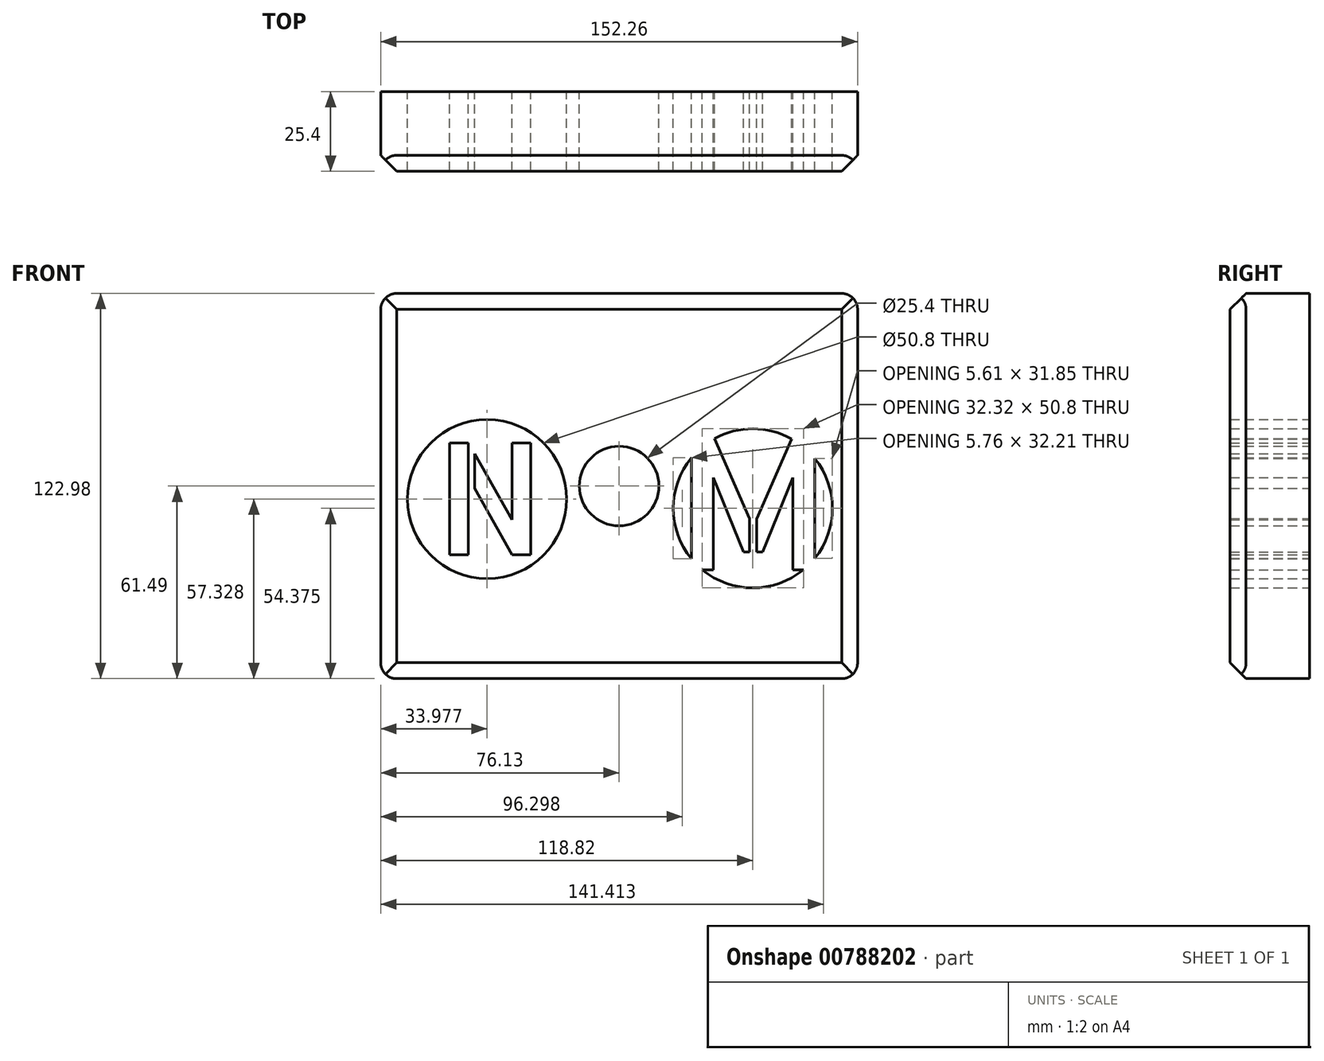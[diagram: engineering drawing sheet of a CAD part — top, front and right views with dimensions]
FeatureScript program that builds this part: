
annotation { "Feature Type Name" : "Feature", "Feature Type Description" : "" }
export const myFeature = defineFeature(function(context is Context, id is Id, definition is map)
    precondition{}
    {
        {
            var Q0;
            Q0=qCreatedBy(makeId("Front.planeOp"),FACE);
            var sketch = newSketch(context, id + "F0", { "sketchPlane" : qUnion([Q0])});
            skLineSegment(sketch, "E0.bottom", {"start": v(-76.13, -61.49) * mm, "end": v(76.13, -61.49) * mm});
            skLineSegment(sketch, "E0.top", {"start": v(-76.13, 61.49) * mm, "end": v(76.13, 61.49) * mm});
            skLineSegment(sketch, "E0.left", {"start": v(-76.13, -61.49) * mm, "end": v(-76.13, 61.49) * mm});
            skLineSegment(sketch, "E0.right", {"start": v(76.13, -61.49) * mm, "end": v(76.13, 61.49) * mm});
            skPoint(sketch, "E0.middle", {"position": v(0, 0) * mm});
            skSolve(sketch);
        }
        {
            var Q0;
            Q0 = qSketchRegion(id + "F0", true);
            extrude(context, id + "F1", {"entities" : qUnion([Q0]), "depth" : 25.4 * mm, "offsetDistance" : 25.4 * mm});
        }
        {
            var Q0;
            Q0=makeQuery(id+"F1.opExtrude","CAP_EDGE",EDGE,{"disambiguationData":[OSD([sQuery(id+"F0.wireOp",EDGE,"E0.left")])],"isStart":false});
            var Q1;
            Q1=makeQuery(id+"F1.opExtrude","CAP_EDGE",EDGE,{"disambiguationData":[OSD([sQuery(id+"F0.wireOp",EDGE,"E0.top")])],"isStart":false});
            var Q2;
            Q2=makeQuery(id+"F1.opExtrude","CAP_EDGE",EDGE,{"disambiguationData":[OSD([sQuery(id+"F0.wireOp",EDGE,"E0.right")])],"isStart":false});
            var Q3;
            Q3=makeQuery(id+"F1.opExtrude","CAP_EDGE",EDGE,{"disambiguationData":[OSD([sQuery(id+"F0.wireOp",EDGE,"E0.bottom")])],"isStart":false});
            chamfer(context, id + "F2", {"entities" : qUnion([Q0, Q1, Q2, Q3]), "width" : 5.08 * mm, "tangentPropagation" : true});
        }
        {
            var Q0;
            Q0=makeQuery(id+"F1.opExtrude","SWEPT_EDGE",EDGE,{"disambiguationData":[OSD([sQuery(id+"F0.wireOp",EDGE,"E0.top"),sQuery(id+"F0.wireOp",EDGE,"E0.left")])]});
            var Q1;
            Q1=makeQuery(id+"F1.opExtrude","SWEPT_EDGE",EDGE,{"disambiguationData":[OSD([sQuery(id+"F0.wireOp",EDGE,"E0.bottom"),sQuery(id+"F0.wireOp",EDGE,"E0.left")])]});
            fillet(context, id + "F3", {"entities" : qUnion([Q0, Q1]), "radius" : 5.08 * mm, "tangentPropagation" : true, "allowEdgeOverflow" : false});
        }
        {
            var Q0;
            Q0=makeQuery(id+"F1.opExtrude","SWEPT_EDGE",EDGE,{"disambiguationData":[OSD([sQuery(id+"F0.wireOp",EDGE,"E0.bottom"),sQuery(id+"F0.wireOp",EDGE,"E0.right")])]});
            var Q1;
            Q1=makeQuery(id+"F1.opExtrude","SWEPT_EDGE",EDGE,{"disambiguationData":[OSD([sQuery(id+"F0.wireOp",EDGE,"E0.top"),sQuery(id+"F0.wireOp",EDGE,"E0.right")])]});
            fillet(context, id + "F4", {"entities" : qUnion([Q0, Q1]), "radius" : 5.08 * mm, "tangentPropagation" : true, "allowEdgeOverflow" : false});
        }
        {
            var Q0;
            Q0=qCreatedBy(makeId("Front.planeOp"),FACE);
            var sketch = newSketch(context, id + "F5", { "sketchPlane" : qUnion([Q0])});
            skCircle(sketch, "E1", {"center": v(0, 0) * mm, "radius": 12.7 * mm});
            skSolve(sketch);
        }
        {
            var Q0;
            Q0=sQuery(id+"F5.wireOp",VERTEX,"E1.center");
            var Q1;
            Q1=makeQuery(id+"F1.opExtrude","SWEPT_BODY",BODY,{"disambiguationData":[OSD([sQuery(id+"F0.wireOp",EDGE,"E0.bottom"),sQuery(id+"F0.wireOp",EDGE,"E0.top"),sQuery(id+"F0.wireOp",EDGE,"E0.left"),sQuery(id+"F0.wireOp",EDGE,"E0.right")])]});
            hole(context, id + "F6", {"style" : HoleStyle.SIMPLE, "endStyle" : HoleEndStyle.THROUGH, "oppositeDirection" : true, "holeDiameter" : 25.4 * mm, "majorDiameter" : 6.35 * mm, "isTappedThrough" : true, "tappedDepth" : 12.7 * mm, "tapClearance" : 3, "locations" : qUnion([Q0]), "scope" : qUnion([Q1])});
        }
        {
            var Q0;
            Q0=qCreatedBy(makeId("Front.planeOp"),FACE);
            var sketch = newSketch(context, id + "F7", { "sketchPlane" : qUnion([Q0])});
            skText(sketch, "E2", { "text": "N", "fontName": "AllertaStencil-Regular.ttf"});
            const initialGuessF7  = {"E2": [-0.05853, -0.02188, 1, 0, 0.0357]};
            skSetInitialGuess(sketch, initialGuessF7);
            skSolve(sketch);
        }
        {
            var Q0;
            Q0=qCreatedBy(makeId("Front.planeOp"),FACE);
            var sketch = newSketch(context, id + "F8", { "sketchPlane" : qUnion([Q0])});
            skCircle(sketch, "E3", {"center": v(-42.15, -4.16) * mm, "radius": 26.44 * mm});
            skSolve(sketch);
        }
        {
            var Q0;
            Q0=sQuery(id+"F8.wireOp",VERTEX,"E3.center");
            var Q1;
            Q1=makeQuery(id+"F1.opExtrude","SWEPT_BODY",BODY,{"disambiguationData":[OSD([sQuery(id+"F0.wireOp",EDGE,"E0.bottom"),sQuery(id+"F0.wireOp",EDGE,"E0.top"),sQuery(id+"F0.wireOp",EDGE,"E0.left"),sQuery(id+"F0.wireOp",EDGE,"E0.right")])]});
            hole(context, id + "F9", {"style" : HoleStyle.SIMPLE, "endStyle" : HoleEndStyle.THROUGH, "oppositeDirection" : true, "holeDiameter" : 50.8 * mm, "majorDiameter" : 6.35 * mm, "isTappedThrough" : true, "tappedDepth" : 12.7 * mm, "tapClearance" : 3, "locations" : qUnion([Q0]), "scope" : qUnion([Q1])});
        }
        {
            var Q0;
            Q0 = qSketchRegion(id + "F7", true);
            extrude(context, id + "F10", {"entities" : qUnion([Q0]), "depth" : 25.4 * mm, "offsetDistance" : 25.4 * mm});
        }
        {
            var Q0;
            Q0=qCreatedBy(makeId("Front.planeOp"),FACE);
            var sketch = newSketch(context, id + "F11", { "sketchPlane" : qUnion([Q0])});
            skText(sketch, "E4", { "text": "M", "fontName": "AllertaStencil-Regular.ttf"});
            const initialGuessF11  = {"E4": [0.01772, -0.02671, 1, 0, 0.04269]};
            skSetInitialGuess(sketch, initialGuessF11);
            skSolve(sketch);
        }
        {
            var Q0;
            Q0=qCreatedBy(makeId("Front.planeOp"),FACE);
            var sketch = newSketch(context, id + "F12", { "sketchPlane" : qUnion([Q0])});
            skCircle(sketch, "E5", {"center": v(42.69, -7.11) * mm, "radius": 28.22 * mm});
            skSolve(sketch);
        }
        {
            var Q0;
            Q0=sQuery(id+"F12.wireOp",VERTEX,"E5.center");
            var Q1;
            Q1=makeQuery(id+"F1.opExtrude","SWEPT_BODY",BODY,{"disambiguationData":[OSD([sQuery(id+"F0.wireOp",EDGE,"E0.bottom"),sQuery(id+"F0.wireOp",EDGE,"E0.top"),sQuery(id+"F0.wireOp",EDGE,"E0.left"),sQuery(id+"F0.wireOp",EDGE,"E0.right")])]});
            hole(context, id + "F13", {"style" : HoleStyle.SIMPLE, "endStyle" : HoleEndStyle.THROUGH, "oppositeDirection" : true, "holeDiameter" : 50.8 * mm, "majorDiameter" : 6.35 * mm, "isTappedThrough" : true, "tappedDepth" : 12.7 * mm, "tapClearance" : 3, "locations" : qUnion([Q0]), "scope" : qUnion([Q1])});
        }
        {
            var Q0;
            Q0 = qSketchRegion(id + "F11", true);
            extrude(context, id + "F14", {"entities" : qUnion([Q0]), "operationType" : NewBodyOperationType.ADD, "depth" : 25.4 * mm, "offsetDistance" : 25.4 * mm});
        }
    });
